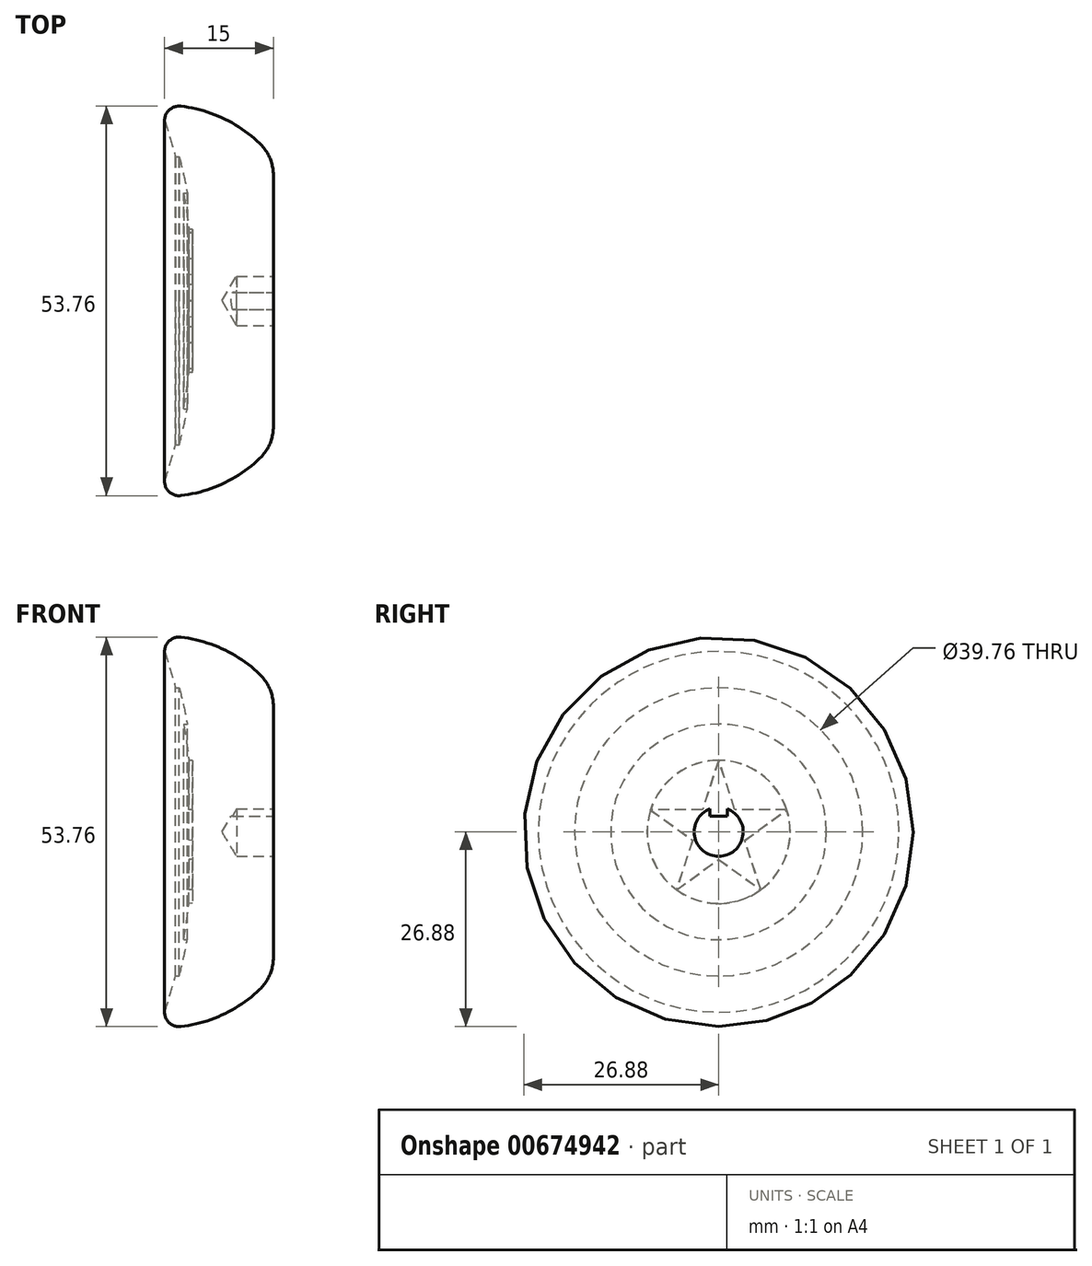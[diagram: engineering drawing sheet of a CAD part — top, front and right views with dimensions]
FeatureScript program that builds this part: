
annotation { "Feature Type Name" : "Feature", "Feature Type Description" : "" }
export const myFeature = defineFeature(function(context is Context, id is Id, definition is map)
    precondition{}
    {
        {
            var Q0;
            Q0=qCreatedBy(makeId("Front.planeOp"),FACE);
            var sketch = newSketch(context, id + "F0", { "sketchPlane" : qUnion([Q0])});
            skLineSegment(sketch, "E0", {"start": v(0, 0) * mm, "end": v(-15, 0) * mm});
            skLineSegment(sketch, "E1", {"start": v(-15, 0) * mm, "end": v(-15, 24.88) * mm});
            skArc(sketch, "E2", {"start": v(-1.85, 21.71) * mm, "mid": v(-6.88, 25.18) * mm, "end": v(-12.76, 26.87) * mm});
            skLineSegment(sketch, "E3", {"start": v(0, 0) * mm, "end": v(0, 17.38) * mm});
            skPoint(sketch, "E4.visualSharp", {"position": v(-15, 27) * mm});
            skArc(sketch, "E4.filletArc", {"start": v(-12.76, 26.87) * mm, "mid": v(-14.33, 26.38) * mm, "end": v(-15, 24.88) * mm});
            skPoint(sketch, "E5.visualSharp", {"position": v(0, 19.66) * mm});
            skArc(sketch, "E5.filletArc", {"start": v(0, 17.38) * mm, "mid": v(-0.48, 19.73) * mm, "end": v(-1.85, 21.71) * mm});
            skLineSegment(sketch, "E6", {"start": v(-15, 0) * mm, "end": v(-11.25, 0) * mm});
            skArc(sketch, "E7", {"start": v(-11.25, 0) * mm, "mid": v(-11.42, 7.47) * mm, "end": v(-12.38, 14.88) * mm});
            skLineSegment(sketch, "E8", {"start": v(-15, 24.88) * mm, "end": v(-15, 19.88) * mm});
            skLineSegment(sketch, "E9", {"start": v(-15, 19.88) * mm, "end": v(-15, 14.88) * mm});
            skLineSegment(sketch, "E10", {"start": v(-15, 14.88) * mm, "end": v(-15, 9.88) * mm});
            skLineSegment(sketch, "E11", {"start": v(-15, 9.88) * mm, "end": v(-11.64, 9.88) * mm});
            skLineSegment(sketch, "E12", {"start": v(-11.64, 9.88) * mm, "end": v(-11.64, 0) * mm});
            skArc(sketch, "E13.0", {"start": v(-10.75, -0.02) * mm, "mid": v(-10.75, 0) * mm, "end": v(-10.75, 0) * mm});
            skLineSegment(sketch, "E14", {"start": v(-15, 14.88) * mm, "end": v(-11.87, 14.88) * mm});
            skLineSegment(sketch, "E15", {"start": v(-15, 19.88) * mm, "end": v(-12.97, 19.88) * mm});
            skArc(sketch, "E16.trimOffspring", {"start": v(-13.5, 19.88) * mm, "mid": v(-14.2, 22.4) * mm, "end": v(-15, 24.88) * mm});
            skArc(sketch, "E17.trimOffspring", {"start": v(-11.87, 14.88) * mm, "mid": v(-12.38, 17.4) * mm, "end": v(-12.97, 19.88) * mm});
            skSolve(sketch);
        }
        {
            var Q0;
            Q0=makeQuery(id+"F0.imprint","IMPRINT",FACE,{"disambiguationData":[TD([[makeQuery(id+"F0.imprint","IMPRINT",EDGE,{"derivedFrom":sQuery(id+"F0.wireOp",EDGE,"E0")}),-1.0]])]});
            var Q1;
            {var subQ3=sQuery(id+"F0.wireOp",EDGE,"E12");Q1=makeQuery(id+"F0.imprint","IMPRINT",FACE,{"disambiguationData":[TD([[makeQuery(id+"F0.imprint","IMPRINT",EDGE,{"derivedFrom":subQ3}),1.0]])]});}
            var Q2;
            Q2=sQuery(id+"F0.wireOp",EDGE,"E0");
            revolve(context, id + "F1", {"entities" : qUnion([Q0, Q1]), "axis" : qUnion([Q2]), "revolveType" : RevolveType.FULL, "surfaceOperationType" : NewSurfaceOperationType.NEW});
        }
        {
            var Q0;
            Q0=makeQuery(id+"F1.opRevolve","SWEPT_FACE",FACE,{"disambiguationData":[OSD([sQuery(id+"F0.wireOp",EDGE,"E3")])]});
            var sketch = newSketch(context, id + "F2", { "sketchPlane" : qUnion([Q0])});
            skPoint(sketch, "E18.0", {"position": v(0, 0) * mm});
            skSolve(sketch);
        }
        {
            var Q0;
            Q0=sQuery(id+"F2.wireOp",VERTEX,"E18.0");
            var Q1;
            Q1=makeQuery(id+"F1.opRevolve","SWEPT_BODY",BODY,{"disambiguationData":[OSD([sQuery(id+"F0.wireOp",EDGE,"E0"),sQuery(id+"F0.wireOp",EDGE,"E1"),sQuery(id+"F0.wireOp",EDGE,"E2"),sQuery(id+"F0.wireOp",EDGE,"E3"),sQuery(id+"F0.wireOp",EDGE,"E4.filletArc"),sQuery(id+"F0.wireOp",EDGE,"E5.filletArc")])]});
            hole(context, id + "F3", {"style" : HoleStyle.SIMPLE, "endStyle" : HoleEndStyle.BLIND, "standardTappedOrClearance" : lookupTablePath({ "standard" : "ANSI", "fit" : "Normal (ASME)", "size" : "1/4", "type" : "Clearance" }), "standardBlindInLast" : lookupTablePath({ "standard" : "ANSI", "fit" : "Free", "size" : "1/4", "type" : "Clearance" }), "holeDiameter" : 6.76 * mm, "majorDiameter" : 6.35 * mm, "holeDepth" : 5.08 * mm, "isTappedThrough" : true, "tappedDepth" : 13.5 * mm, "tapClearance" : 3, "startFromSketch" : true, "locations" : qUnion([Q0]), "scope" : qUnion([Q1])});
        }
        {
            var Q0;
            Q0=makeQuery(id+"F1.opRevolve","SWEPT_FACE",FACE,{"disambiguationData":[OSD([sQuery(id+"F0.wireOp",EDGE,"E3")])]});
            var sketch = newSketch(context, id + "F4", { "sketchPlane" : qUnion([Q0])});
            skLineSegment(sketch, "E19.bottom", {"start": v(1.2, 2.19) * mm, "end": v(-1.2, 2.19) * mm});
            skLineSegment(sketch, "E19.top", {"start": v(1.2, 4.57) * mm, "end": v(-1.2, 4.57) * mm});
            skLineSegment(sketch, "E19.left", {"start": v(1.2, 2.19) * mm, "end": v(1.2, 4.57) * mm});
            skLineSegment(sketch, "E19.right", {"start": v(-1.2, 2.19) * mm, "end": v(-1.2, 4.57) * mm});
            skPoint(sketch, "E19.middle", {"position": v(0, 3.38) * mm});
            skSolve(sketch);
        }
        {
            var Q0;
            {var subQ0=sQuery(id+"F4.wireOp",EDGE,"E19.bottom");Q0=makeQuery(id+"F4.imprint","IMPRINT",FACE,{"disambiguationData":[TD([[makeQuery(id+"F4.imprint","IMPRINT",EDGE,{"derivedFrom":subQ0}),-1.0]])]});}
            extrude(context, id + "F5", {"entities" : qUnion([Q0]), "operationType" : NewBodyOperationType.ADD, "endBound" : BoundingType.UP_TO_NEXT, "oppositeDirection" : true, "depth" : 25 * mm, "offsetDistance" : 25 * mm});
        }
        {
            var Q0;
            Q0=makeQuery(id+"F1.opRevolve","SWEPT_FACE",FACE,{"disambiguationData":[OSD([sQuery(id+"F0.wireOp",EDGE,"E12")])]});
            var sketch = newSketch(context, id + "F6", { "sketchPlane" : qUnion([Q0])});
            skLineSegment(sketch, "E20", {"start": v(0, 0) * mm, "end": v(0, 9.88) * mm});
            skLineSegment(sketch, "E21", {"start": v(0, 9.88) * mm, "end": v(-5.8, -8) * mm});
            skCircle(sketch, "E22.0.0", {"center": v(0, 0) * mm, "radius": 9.88 * mm});
            skLineSegment(sketch, "E23.1.0", {"start": v(-9.4, 3.05) * mm, "end": v(5.8, -8) * mm});
            skLineSegment(sketch, "E23.2.0", {"start": v(-5.8, -8) * mm, "end": v(9.4, 3.05) * mm});
            skLineSegment(sketch, "E23.3.0", {"start": v(5.8, -8) * mm, "end": v(0, 9.88) * mm});
            skLineSegment(sketch, "E23.4.0", {"start": v(9.4, 3.05) * mm, "end": v(-9.4, 3.05) * mm});
            skSolve(sketch);
        }
        {
            var Q0;
            {var subQ0=sQuery(id+"F6.wireOp",EDGE,"E23.3.0");var subQ3=sQuery(id+"F6.wireOp",EDGE,"E23.4.0");var subQ5=makeQuery(id+"F6.imprint","INTERSECT",VERTEX,{"derivedFrom":[subQ0,subQ3]});Q0=makeQuery(id+"F6.imprint","IMPRINT",FACE,{"disambiguationData":[TD([[makeQuery(id+"F6.imprint","IMPRINT",EDGE,{"disambiguationData":[TD([[subQ5,1.0]])],"derivedFrom":subQ3}),-1.0]])]});}
            var Q1;
            {var subQ1=sQuery(id+"F6.wireOp",EDGE,"E21");var subQ3=sQuery(id+"F6.wireOp",EDGE,"E23.1.0");var subQ4=makeQuery(id+"F6.imprint","INTERSECT",VERTEX,{"derivedFrom":[subQ1,subQ3]});Q1=makeQuery(id+"F6.imprint","IMPRINT",FACE,{"disambiguationData":[TD([[makeQuery(id+"F6.imprint","IMPRINT",EDGE,{"disambiguationData":[TD([[subQ4,-1.0]])],"derivedFrom":subQ1}),-1.0]])]});}
            var Q2;
            {var subQ0=sQuery(id+"F6.wireOp",EDGE,"E23.2.0");var subQ3=sQuery(id+"F6.wireOp",EDGE,"E23.1.0");var subQ5=makeQuery(id+"F6.imprint","INTERSECT",VERTEX,{"derivedFrom":[subQ3,subQ0]});Q2=makeQuery(id+"F6.imprint","IMPRINT",FACE,{"disambiguationData":[TD([[makeQuery(id+"F6.imprint","IMPRINT",EDGE,{"disambiguationData":[TD([[subQ5,-1.0]])],"derivedFrom":subQ3}),-1.0]])]});}
            var Q3;
            {var subQ0=sQuery(id+"F6.wireOp",EDGE,"E23.3.0");var subQ3=sQuery(id+"F6.wireOp",EDGE,"E23.2.0");var subQ5=makeQuery(id+"F6.imprint","INTERSECT",VERTEX,{"derivedFrom":[subQ3,subQ0]});Q3=makeQuery(id+"F6.imprint","IMPRINT",FACE,{"disambiguationData":[TD([[makeQuery(id+"F6.imprint","IMPRINT",EDGE,{"disambiguationData":[TD([[subQ5,-1.0]])],"derivedFrom":subQ3}),-1.0]])]});}
            var Q4;
            {var subQ1=sQuery(id+"F6.wireOp",EDGE,"E21");var subQ3=sQuery(id+"F6.wireOp",EDGE,"E23.4.0");var subQ4=makeQuery(id+"F6.imprint","INTERSECT",VERTEX,{"derivedFrom":[subQ1,subQ3]});Q4=makeQuery(id+"F6.imprint","IMPRINT",FACE,{"disambiguationData":[TD([[makeQuery(id+"F6.imprint","IMPRINT",EDGE,{"disambiguationData":[TD([[subQ4,-1.0]])],"derivedFrom":subQ3}),-1.0]])]});}
            extrude(context, id + "F7", {"entities" : qUnion([Q0, Q1, Q2, Q3, Q4]), "operationType" : NewBodyOperationType.REMOVE, "oppositeDirection" : true, "depth" : .5 * mm, "offsetDistance" : 25 * mm, "hasDraft" : true, "draftAngle" : 3 * degree, "draftPullDirection" : true});
        }
    });
